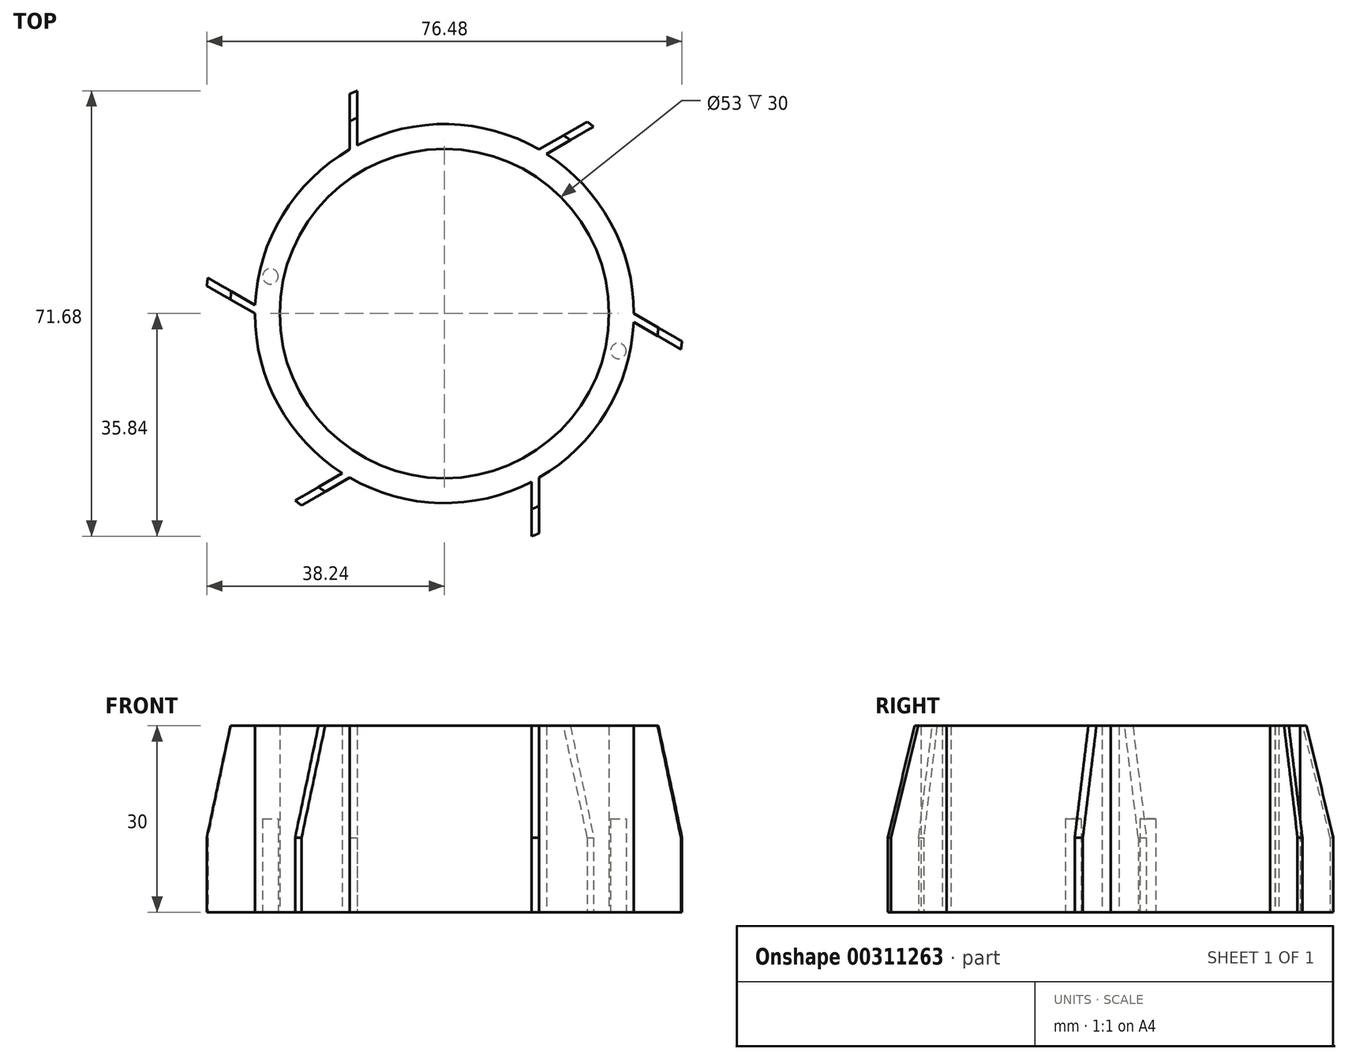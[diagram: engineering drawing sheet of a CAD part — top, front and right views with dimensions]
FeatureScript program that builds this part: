
annotation { "Feature Type Name" : "Feature", "Feature Type Description" : "" }
export const myFeature = defineFeature(function(context is Context, id is Id, definition is map)
    precondition{}
    {
        {
            var Q0;
            Q0=qCreatedBy(makeId("Front.planeOp"),FACE);
            var sketch = newSketch(context, id + "F0", { "sketchPlane" : qUnion([Q0])});
            skLineSegment(sketch, "E0", {"start": v(26.5, 30) * mm, "end": v(26.5, 0) * mm});
            skLineSegment(sketch, "E1", {"start": v(26.5, 0) * mm, "end": v(38.5, 0) * mm});
            skLineSegment(sketch, "E2", {"start": v(38.5, 0) * mm, "end": v(38.5, 12) * mm});
            skLineSegment(sketch, "E3", {"start": v(38.5, 12) * mm, "end": v(34.5, 30) * mm});
            skLineSegment(sketch, "E4", {"start": v(34.5, 30) * mm, "end": v(26.5, 30) * mm});
            skLineSegment(sketch, "E5", {"start": v(0, 0) * mm, "end": v(0, 42.95) * mm, "construction": true});
            skSolve(sketch);
        }
        {
            var Q0;
            Q0=makeQuery(id+"F0.imprint","IMPRINT",FACE,{"disambiguationData":[TD([[makeQuery(id+"F0.imprint","IMPRINT",EDGE,{"derivedFrom":sQuery(id+"F0.wireOp",EDGE,"E0")}),1.0]])]});
            var Q1;
            Q1=sQuery(id+"F0.wireOp",EDGE,"E5");
            revolve(context, id + "F1", {"entities" : qUnion([Q0]), "axis" : qUnion([Q1]), "revolveType" : RevolveType.FULL});
        }
        {
            var Q0;
            Q0=makeQuery(id+"F1.opRevolve","SWEPT_FACE",FACE,{"disambiguationData":[OSD([sQuery(id+"F0.wireOp",EDGE,"E1")])]});
            var sketch = newSketch(context, id + "F2", { "sketchPlane" : qUnion([Q0])});
            skCircle(sketch, "E6", {"center": v(-28, -6) * mm, "radius": 1.25 * mm});
            skCircle(sketch, "E7", {"center": v(28, 6) * mm, "radius": 1.25 * mm});
            skSolve(sketch);
        }
        {
            var Q0;
            Q0 = qSketchRegion(id + "F2", true);
            extrude(context, id + "F3", {"entities" : qUnion([Q0]), "operationType" : NewBodyOperationType.REMOVE, "oppositeDirection" : true, "depth" : 15 * mm});
        }
        {
            var Q0;
            Q0=makeQuery(id+"F1.opRevolve","SWEPT_FACE",FACE,{"disambiguationData":[OSD([sQuery(id+"F0.wireOp",EDGE,"E1")])]});
            var sketch = newSketch(context, id + "F4", { "sketchPlane" : qUnion([Q0])});
            skArc(sketch, "E8", {"start": v(-30.5, 0) * mm, "mid": v(-26.75, 14.65) * mm, "end": v(-16.42, 25.7) * mm});
            skLineSegment(sketch, "E9", {"start": v(-30.5, 0) * mm, "end": v(-48.07, -10.14) * mm});
            skLineSegment(sketch, "E10", {"start": v(-33.74, 35.7) * mm, "end": v(-16.42, 25.7) * mm});
            skArc(sketch, "E11", {"start": v(-48.07, -10.14) * mm, "mid": v(-46.89, 14.65) * mm, "end": v(-33.74, 35.7) * mm});
            skLineSegment(sketch, "E12.1.0", {"start": v(-47.79, -11.37) * mm, "end": v(-30.47, -1.37) * mm});
            skArc(sketch, "E12.1.1", {"start": v(-15.25, -46.7) * mm, "mid": v(-36.13, -33.28) * mm, "end": v(-47.79, -11.37) * mm});
            skLineSegment(sketch, "E12.1.2", {"start": v(-15.25, -26.41) * mm, "end": v(-15.25, -46.7) * mm});
            skArc(sketch, "E12.1.3", {"start": v(-15.25, -26.41) * mm, "mid": v(-26.07, -15.84) * mm, "end": v(-30.47, -1.37) * mm});
            skLineSegment(sketch, "E12.2.0", {"start": v(-14.05, -47.07) * mm, "end": v(-14.05, -27.07) * mm});
            skArc(sketch, "E12.2.1", {"start": v(32.82, -36.55) * mm, "mid": v(10.76, -47.93) * mm, "end": v(-14.05, -47.07) * mm});
            skLineSegment(sketch, "E12.2.2", {"start": v(15.25, -26.41) * mm, "end": v(32.82, -36.55) * mm});
            skArc(sketch, "E12.2.3", {"start": v(15.25, -26.41) * mm, "mid": v(0.68, -30.5) * mm, "end": v(-14.05, -27.07) * mm});
            skLineSegment(sketch, "E12.3.0", {"start": v(33.74, -35.7) * mm, "end": v(16.42, -25.7) * mm});
            skArc(sketch, "E12.3.1", {"start": v(48.07, 10.14) * mm, "mid": v(46.89, -14.65) * mm, "end": v(33.74, -35.7) * mm});
            skLineSegment(sketch, "E12.3.2", {"start": v(30.5, 0) * mm, "end": v(48.07, 10.14) * mm});
            skArc(sketch, "E12.3.3", {"start": v(30.5, 0) * mm, "mid": v(26.75, -14.65) * mm, "end": v(16.42, -25.7) * mm});
            skLineSegment(sketch, "E12.4.0", {"start": v(47.79, 11.37) * mm, "end": v(30.47, 1.37) * mm});
            skArc(sketch, "E12.4.1", {"start": v(15.25, 46.7) * mm, "mid": v(36.13, 33.28) * mm, "end": v(47.79, 11.37) * mm});
            skLineSegment(sketch, "E12.4.2", {"start": v(15.25, 26.41) * mm, "end": v(15.25, 46.7) * mm});
            skArc(sketch, "E12.4.3", {"start": v(15.25, 26.41) * mm, "mid": v(26.07, 15.84) * mm, "end": v(30.47, 1.37) * mm});
            skLineSegment(sketch, "E12.5.0", {"start": v(14.05, 47.07) * mm, "end": v(14.05, 27.07) * mm});
            skArc(sketch, "E12.5.1", {"start": v(-32.82, 36.55) * mm, "mid": v(-10.76, 47.93) * mm, "end": v(14.05, 47.07) * mm});
            skLineSegment(sketch, "E12.5.2", {"start": v(-15.25, 26.41) * mm, "end": v(-32.82, 36.55) * mm});
            skArc(sketch, "E12.5.3", {"start": v(-15.25, 26.41) * mm, "mid": v(-0.68, 30.5) * mm, "end": v(14.05, 27.07) * mm});
            skSolve(sketch);
        }
        {
            var Q0;
            Q0 = qSketchRegion(id + "F4", true);
            extrude(context, id + "F5", {"entities" : qUnion([Q0]), "operationType" : NewBodyOperationType.REMOVE, "endBound" : BoundingType.THROUGH_ALL, "oppositeDirection" : true, "depth" : 25 * mm});
        }
    });
